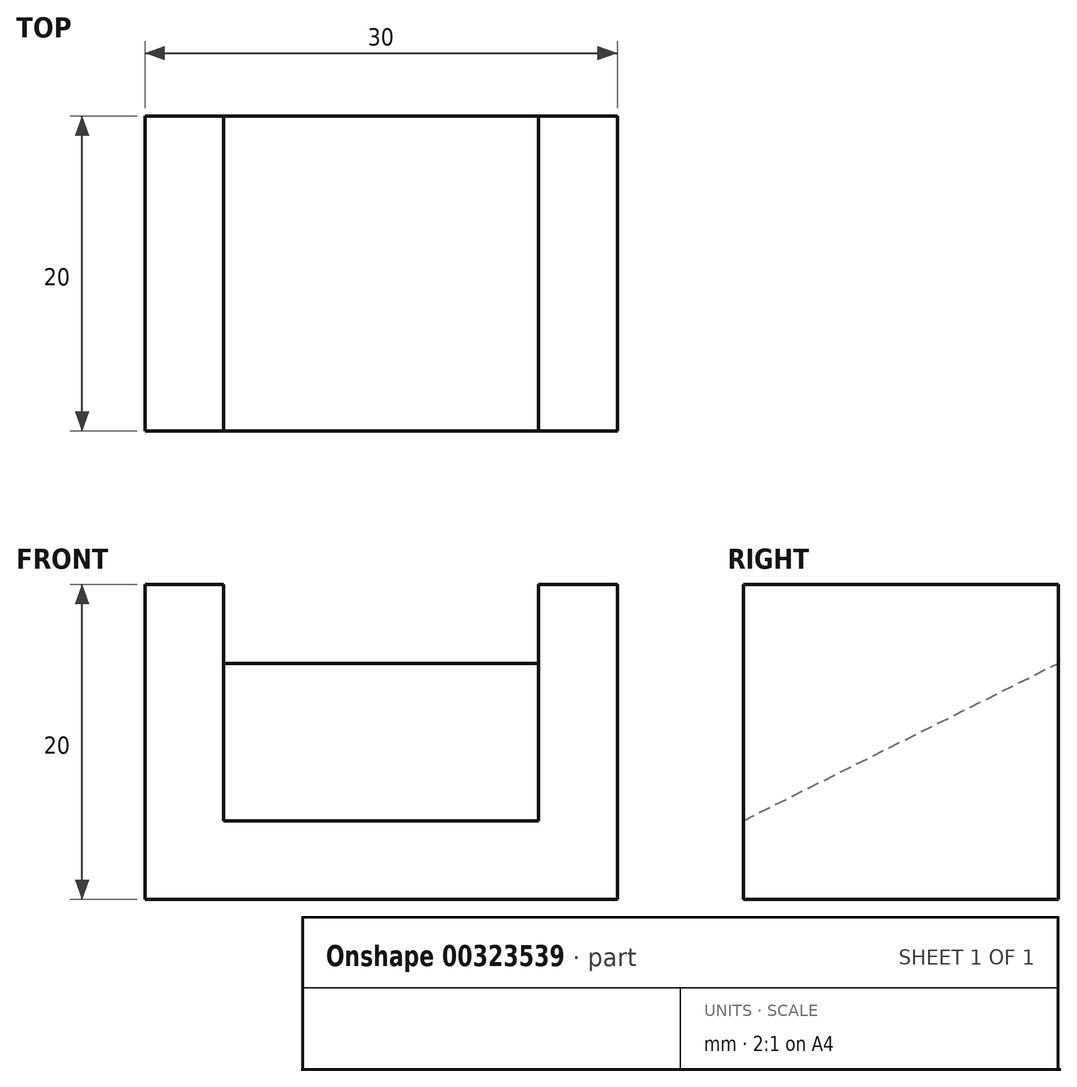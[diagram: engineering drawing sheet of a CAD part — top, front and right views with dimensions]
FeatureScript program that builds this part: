
annotation { "Feature Type Name" : "Feature", "Feature Type Description" : "" }
export const myFeature = defineFeature(function(context is Context, id is Id, definition is map)
    precondition{}
    {
        {
            var Q0;
            Q0=qCreatedBy(makeId("Front.planeOp"),FACE);
            var sketch = newSketch(context, id + "F0", { "sketchPlane" : qUnion([Q0])});
            skLineSegment(sketch, "E0", {"start": v(-15, 0) * mm, "end": v(-15, 20) * mm});
            skLineSegment(sketch, "E1", {"start": v(-15, 20) * mm, "end": v(-10, 20) * mm});
            skLineSegment(sketch, "E2", {"start": v(-10, 20) * mm, "end": v(-10, 5) * mm});
            skLineSegment(sketch, "E3", {"start": v(-10, 5) * mm, "end": v(10, 5) * mm});
            skLineSegment(sketch, "E4", {"start": v(10, 5) * mm, "end": v(10, 20) * mm});
            skLineSegment(sketch, "E5", {"start": v(10, 20) * mm, "end": v(15, 20) * mm});
            skLineSegment(sketch, "E6", {"start": v(15, 20) * mm, "end": v(15, 0) * mm});
            skLineSegment(sketch, "E7", {"start": v(15, 0) * mm, "end": v(-15, 0) * mm});
            skSolve(sketch);
        }
        {
            var Q0;
            Q0=makeQuery(id+"F0.imprint","IMPRINT",FACE,{"disambiguationData":[TD([[makeQuery(id+"F0.imprint","IMPRINT",EDGE,{"derivedFrom":sQuery(id+"F0.wireOp",EDGE,"E0")}),-1.0]])]});
            extrude(context, id + "F1", {"entities" : qUnion([Q0]), "oppositeDirection" : true, "depth" : 20 * mm});
        }
        {
            var Q0;
            Q0=makeQuery(id+"F1.opExtrude","SWEPT_FACE",FACE,{"disambiguationData":[OSD([sQuery(id+"F0.wireOp",EDGE,"E6")])]});
            var sketch = newSketch(context, id + "F2", { "sketchPlane" : qUnion([Q0])});
            skLineSegment(sketch, "E8", {"start": v(0, 5) * mm, "end": v(20, 15) * mm});
            skLineSegment(sketch, "E9", {"start": v(20, 15) * mm, "end": v(20, 5) * mm});
            skLineSegment(sketch, "E10", {"start": v(0, 5) * mm, "end": v(20, 5) * mm});
            skSolve(sketch);
        }
        {
            var Q0;
            Q0=makeQuery(id+"F2.imprint","IMPRINT",FACE,{"disambiguationData":[TD([[makeQuery(id+"F2.imprint","IMPRINT",EDGE,{"derivedFrom":sQuery(id+"F2.wireOp",EDGE,"E8")}),-1.0]])]});
            extrude(context, id + "F3", {"entities" : qUnion([Q0]), "operationType" : NewBodyOperationType.ADD, "oppositeDirection" : true, "depth" : 25 * mm});
        }
    });
